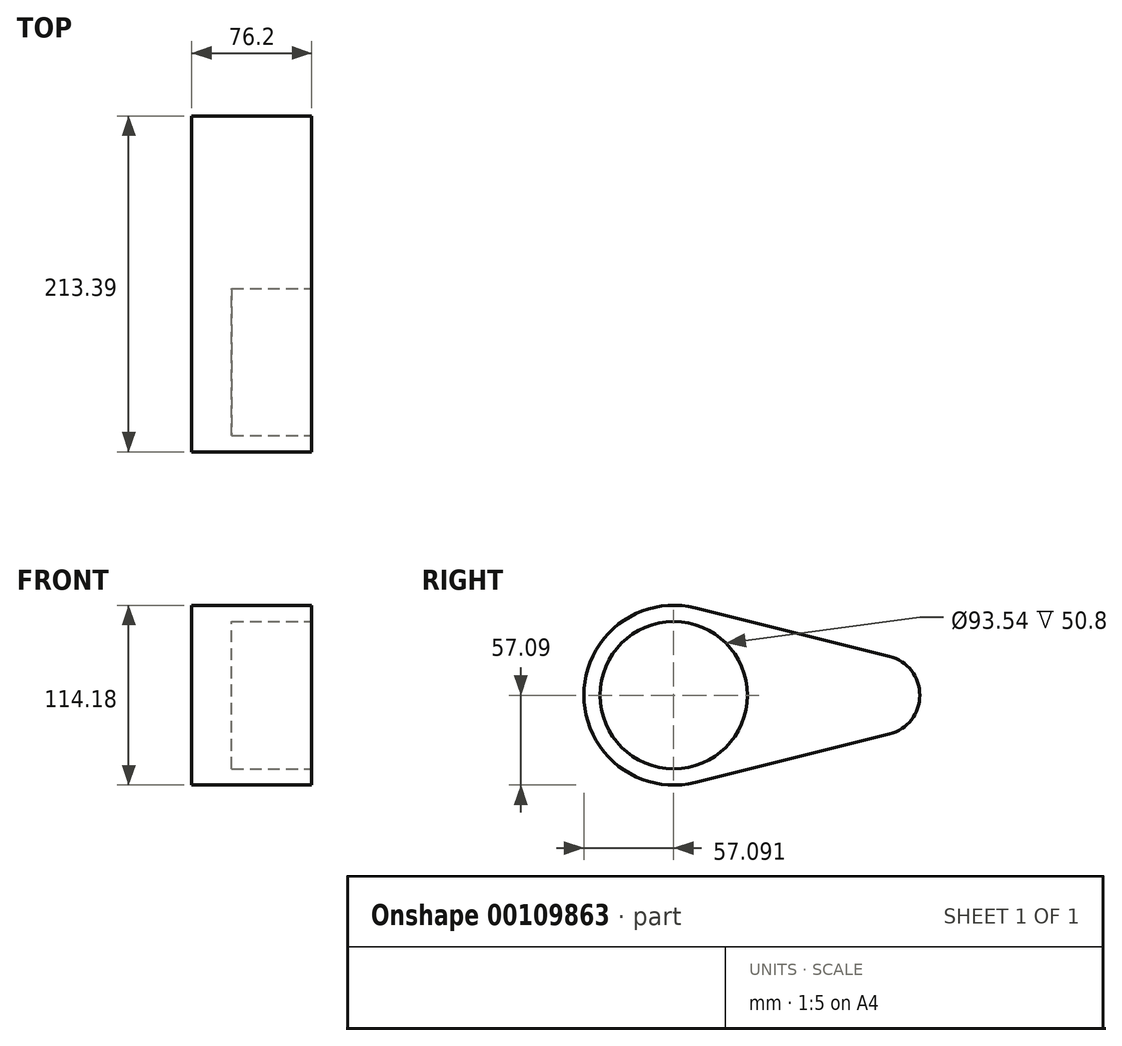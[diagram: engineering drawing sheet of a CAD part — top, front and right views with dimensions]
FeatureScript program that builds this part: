
annotation { "Feature Type Name" : "Feature", "Feature Type Description" : "" }
export const myFeature = defineFeature(function(context is Context, id is Id, definition is map)
    precondition{}
    {
        {
            var Q0;
            Q0=qCreatedBy(makeId("Right.planeOp"),FACE);
            var sketch = newSketch(context, id + "F0", { "sketchPlane" : qUnion([Q0])});
            skCircle(sketch, "E0", {"center": v(-61.58, 0) * mm, "radius": 57.1 * mm});
            skCircle(sketch, "E1", {"center": v(69.32, 0) * mm, "radius": 25.4 * mm});
            skLineSegment(sketch, "E2", {"start": v(-47.76, 55.4) * mm, "end": v(75.47, 24.64) * mm});
            skLineSegment(sketch, "E3", {"start": v(-47.76, -55.4) * mm, "end": v(75.47, -24.64) * mm});
            skSolve(sketch);
        }
        {
            var Q0;
            Q0 = qSketchRegion(id + "F0", true);
            extrude(context, id + "F1", {"entities" : qUnion([Q0]), "depth" : 76.2 * mm});
        }
        {
            var Q0;
            Q0=makeQuery(id+"F1.opExtrude","CAP_FACE",FACE,{"disambiguationData":[OSD([sQuery(id+"F0.wireOp",EDGE,"E0"),sQuery(id+"F0.wireOp",EDGE,"E1"),sQuery(id+"F0.wireOp",EDGE,"E2"),sQuery(id+"F0.wireOp",EDGE,"E3")])],"isStart":false});
            var sketch = newSketch(context, id + "F2", { "sketchPlane" : qUnion([Q0])});
            skCircle(sketch, "E4", {"center": v(-61.58, 0) * mm, "radius": 46.77 * mm});
            skSolve(sketch);
        }
        {
            var Q0;
            Q0=makeQuery(id+"F2.imprint","IMPRINT",FACE,{"disambiguationData":[TD([[makeQuery(id+"F2.imprint","IMPRINT",EDGE,{"derivedFrom":sQuery(id+"F2.wireOp",EDGE,"E4")}),1.0]])]});
            extrude(context, id + "F3", {"entities" : qUnion([Q0]), "operationType" : NewBodyOperationType.REMOVE, "oppositeDirection" : true, "depth" : 50.8 * mm});
        }
    });
